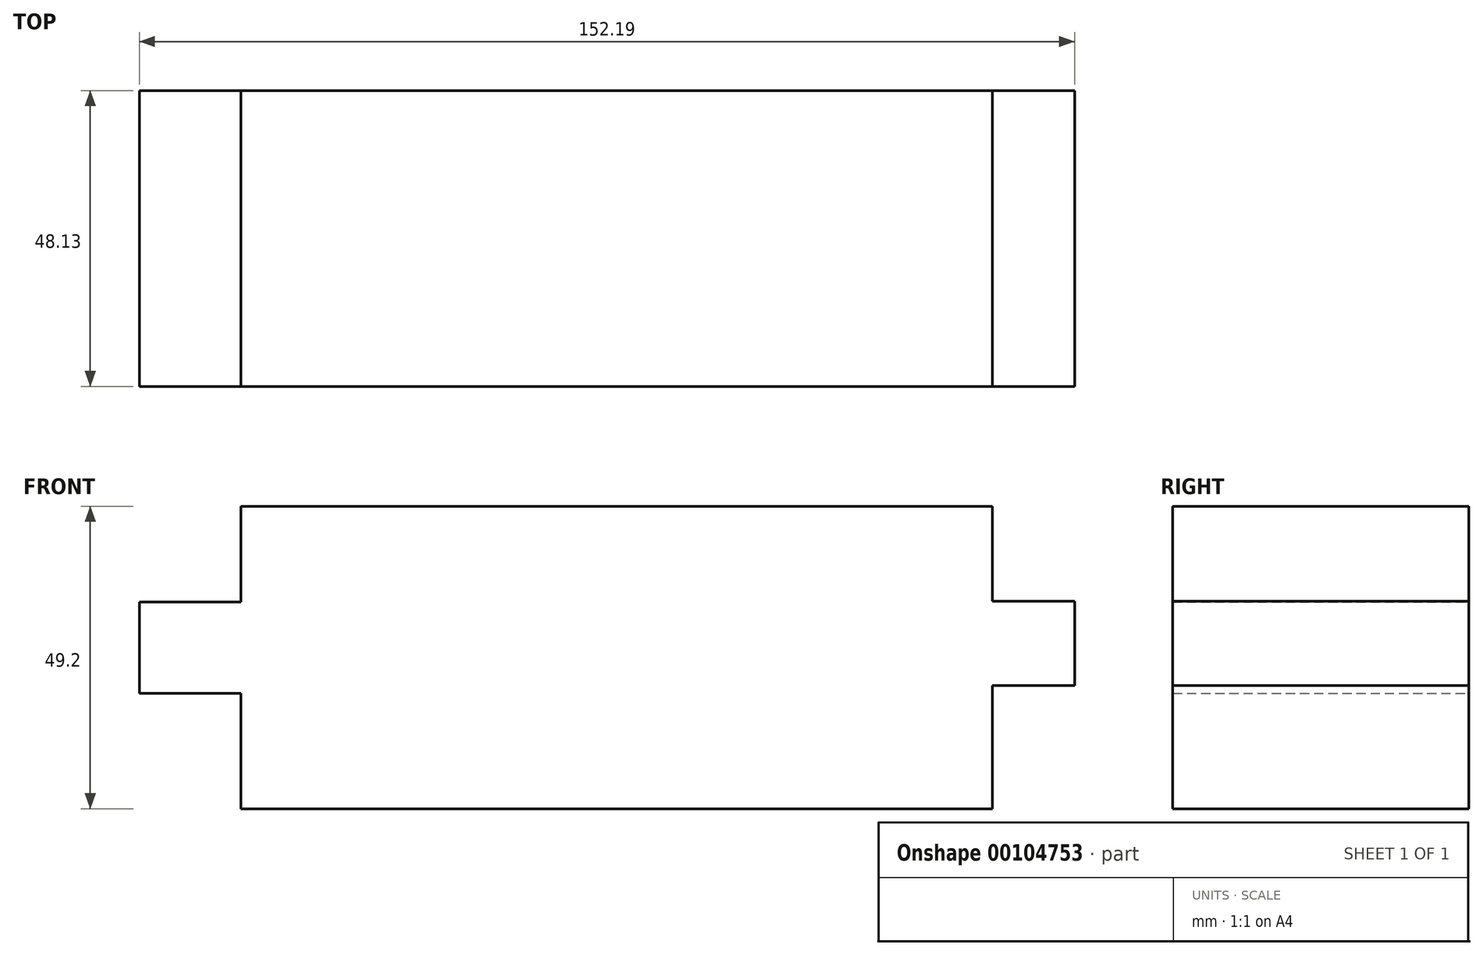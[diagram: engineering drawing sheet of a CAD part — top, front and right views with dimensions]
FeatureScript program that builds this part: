
annotation { "Feature Type Name" : "Feature", "Feature Type Description" : "" }
export const myFeature = defineFeature(function(context is Context, id is Id, definition is map)
    precondition{}
    {
        {
            var Q0;
            Q0=qCreatedBy(makeId("Front.planeOp"),FACE);
            var sketch = newSketch(context, id + "F0", { "sketchPlane" : qUnion([Q0])});
            skLineSegment(sketch, "E0.bottom", {"start": v(61.14, 24.6) * mm, "end": v(-61.14, 24.6) * mm});
            skLineSegment(sketch, "E0.top", {"start": v(61.14, -24.6) * mm, "end": v(-61.14, -24.6) * mm});
            skPoint(sketch, "E0.middle", {"position": v(0, 0) * mm});
            skLineSegment(sketch, "E1", {"start": v(-61.14, 9.04) * mm, "end": v(-77.66, 9.04) * mm});
            skLineSegment(sketch, "E2", {"start": v(-77.66, 9.04) * mm, "end": v(-77.66, -5.8) * mm});
            skLineSegment(sketch, "E3", {"start": v(-77.66, -5.8) * mm, "end": v(-61.14, -5.8) * mm});
            skLineSegment(sketch, "E4", {"start": v(61.14, 9.17) * mm, "end": v(74.53, 9.17) * mm});
            skLineSegment(sketch, "E5", {"start": v(74.53, 9.17) * mm, "end": v(74.53, -4.53) * mm});
            skLineSegment(sketch, "E6", {"start": v(74.53, -4.53) * mm, "end": v(61.14, -4.53) * mm});
            skLineSegment(sketch, "E7", {"start": v(-61.14, 24.6) * mm, "end": v(-61.14, 9.04) * mm});
            skLineSegment(sketch, "E8", {"start": v(-61.14, -5.8) * mm, "end": v(-61.14, -24.6) * mm});
            skLineSegment(sketch, "E9", {"start": v(61.14, 24.6) * mm, "end": v(61.14, 9.17) * mm});
            skLineSegment(sketch, "E10", {"start": v(61.14, -4.53) * mm, "end": v(61.14, -24.6) * mm});
            skSolve(sketch);
        }
        {
            var Q0;
            Q0=makeQuery(id+"F0.imprint","IMPRINT",FACE,{"disambiguationData":[TD([[makeQuery(id+"F0.imprint","IMPRINT",EDGE,{"derivedFrom":sQuery(id+"F0.wireOp",EDGE,"E0.bottom")}),1.0]])]});
            extrude(context, id + "F1", {"entities" : qUnion([Q0]), "depth" : 48.13 * mm});
        }
    });
